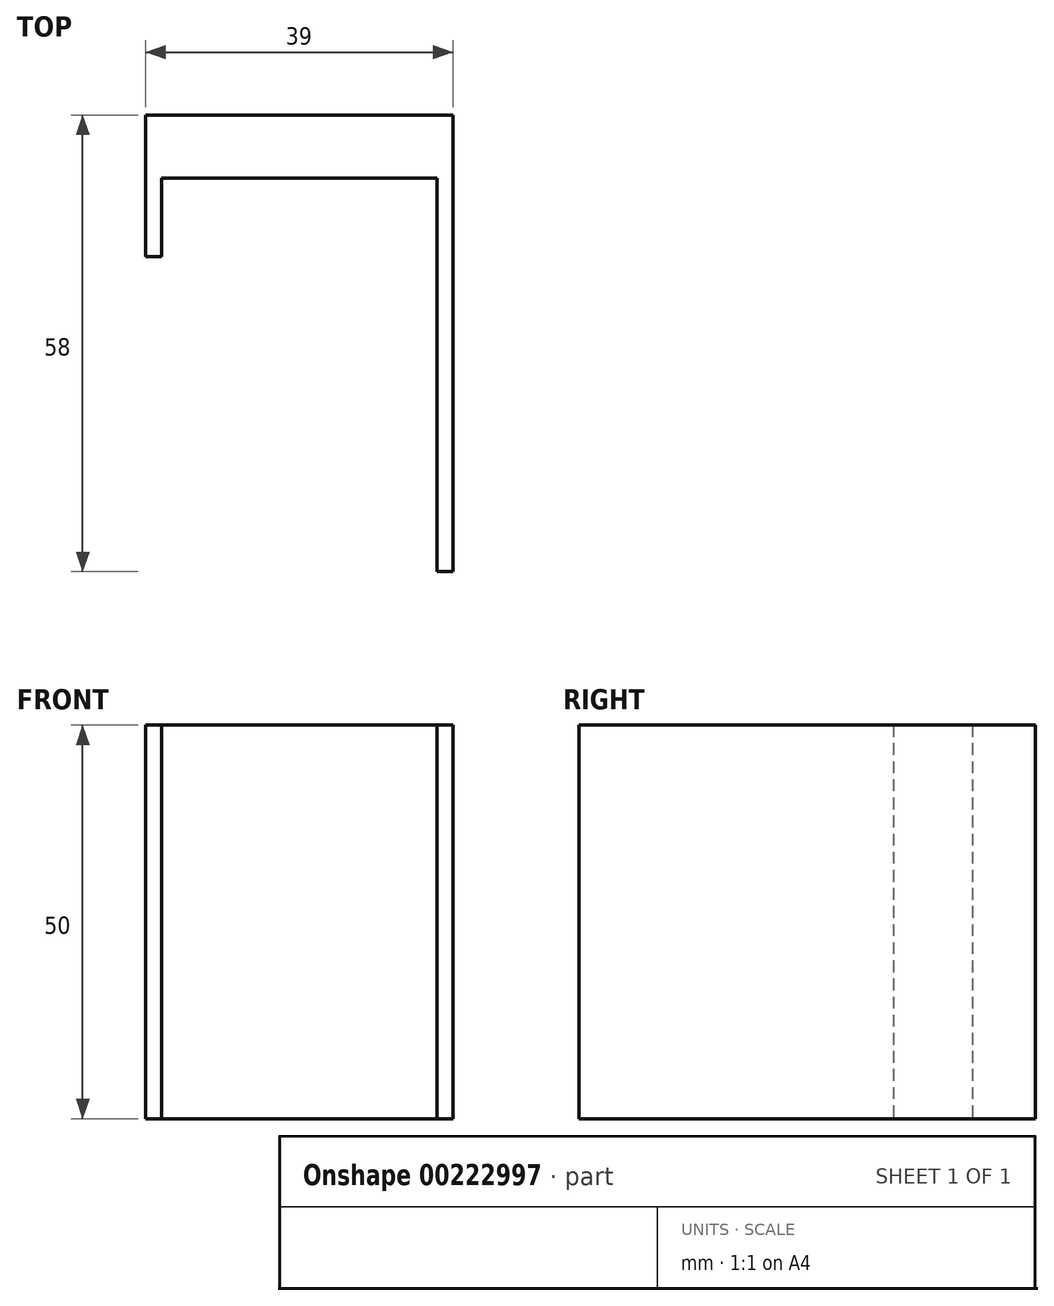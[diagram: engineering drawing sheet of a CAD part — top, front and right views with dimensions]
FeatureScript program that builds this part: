
annotation { "Feature Type Name" : "Feature", "Feature Type Description" : "" }
export const myFeature = defineFeature(function(context is Context, id is Id, definition is map)
    precondition{}
    {
        {
            var Q0;
            Q0=qCreatedBy(makeId("Top.planeOp"),FACE);
            var sketch = newSketch(context, id + "F0", { "sketchPlane" : qUnion([Q0])});
            skLineSegment(sketch, "E0", {"start": v(-17.82, 19.99) * mm, "end": v(17.18, 19.99) * mm});
            skLineSegment(sketch, "E1", {"start": v(-17.82, 19.99) * mm, "end": v(-17.82, 9.99) * mm});
            skLineSegment(sketch, "E2", {"start": v(17.18, 19.99) * mm, "end": v(17.18, -30.01) * mm});
            skLineSegment(sketch, "E3.0", {"start": v(-19.82, 20.12) * mm, "end": v(-19.82, 9.99) * mm});
            skLineSegment(sketch, "E4.0", {"start": v(-17.81, 27.99) * mm, "end": v(17.15, 27.99) * mm});
            skLineSegment(sketch, "E5.0", {"start": v(19.18, 20.12) * mm, "end": v(19.18, -30.01) * mm});
            skLineSegment(sketch, "E6", {"start": v(-19.82, 9.99) * mm, "end": v(-17.82, 9.99) * mm});
            skLineSegment(sketch, "E7", {"start": v(-19.82, 20.12) * mm, "end": v(-19.82, 27.99) * mm});
            skLineSegment(sketch, "E8", {"start": v(-17.81, 27.99) * mm, "end": v(-19.82, 27.99) * mm});
            skLineSegment(sketch, "E9", {"start": v(17.15, 27.99) * mm, "end": v(19.18, 27.99) * mm});
            skLineSegment(sketch, "E10", {"start": v(19.18, 27.99) * mm, "end": v(19.18, 20.12) * mm});
            skLineSegment(sketch, "E11", {"start": v(17.18, -30.01) * mm, "end": v(19.18, -30.01) * mm});
            skSolve(sketch);
        }
        {
            var Q0;
            Q0=makeQuery(id+"F0.imprint","IMPRINT",FACE,{"disambiguationData":[TD([[makeQuery(id+"F0.imprint","IMPRINT",EDGE,{"derivedFrom":sQuery(id+"F0.wireOp",EDGE,"E0")}),1.0]])]});
            extrude(context, id + "F1", {"entities" : qUnion([Q0]), "depth" : 50 * mm});
        }
    });
